# Revit family: RN 32030 Set di allacciamento
name_source: partatom
category: Rohrzubehör
units: mm (PartAtom-declared; Revit-internal decimal feet)

## family parameters
Arbeitsebenenbasiert = Nein
Beim Laden mit Abzugskörper schneiden = Nein
Bemaßung runder Anschluss = Durchmesser verwenden
Gemeinsam genutzt = Nein
Immer vertikal = Ja
Teiletyp = Ventil - Zerlegung in

## types (2) — shared parameters
1.010.00.2 Blattnummer der Richtlinie = 17
1.010.00.3 Ausgabedatum (Monat) der Richtlinie = 201601
1.010.00.4 Herstellername = R. Nussbaum AG
1.010.00.5 Revisionsdatum der Datei = 20190528
1.010.00.6 Webadresse des Herstellers = http://www.nussbaum.ch
1.100.00.3 Sortiernummer für Anzeigereihenfolge = 10
1.100.00.4 Produktbezeichnung = Wasseraufbereitungsarmaturen
1.960/3L.00.8 Link (URL) = https://www.nussbaum.ch
17.700.00.4 Armaturentyp = 1
17.700.00.6 kvs-Wert [m3/h] = 3
17.700.00.7 Maximale Betriebstemperatur TB [°C] = 60
17.700.00.8 Maximaler Betriebsdruck (Arbeitsdruck) ps [1.0 · 105 Pa] = 16
CONNECTOR0_dZ_01 = 70 mm  [stored 0.229659 ft]
CONNECTOR1_dX_00 = 70 mm  [stored 0.229659 ft]
CONNECTOR1_ref_dX = 70 mm  [stored 0.229659 ft]
Connector Visibility = Nein
EnclosingSpace Visibility = Nein
Hersteller = R. Nussbauzm AG
URL = https://www.nussbaum.ch

## per-type parameters (varying)
| type | 1.800.00.3 TGA-Nummer | 1.810.00.3 Hersteller-Bestellnummer | 1.810.00.4 DATANORM-Nummer | 1.810.00.5 StLB-Nummer | 1.810.00.6 GTIN-Nummer | 17.700.00.30 Produktbeschreibung | 17.700.00.5 Nennweite DN | CONNECTOR0_DIAMETER_dZ_0r | CONNECTOR0_dZ_00 | CONNECTOR0_ref_dZ | CONNECTOR1_DIAMETER_dX_0r | CONNECTOR1_dX_01 | Modell | R. Nussbaum AG 32030.06 de Visibility | R. Nussbaum AG 32030.07 de Visibility | Typenkommentare |
| DN 25 | 01000200000000000000000000000200700000000000000001???00000 | 32030.06 | 32030.06 | 618.165 | 7612945007513 | 32030.06, Anschlussgarnitur, zu Stand-Wassererwärmer, DN=25, Rp=1 | 25 | 25 mm  [stored 0.082021 ft] | 53 mm | 53 mm | 40 mm | 59 mm | 32030.06 | Ja | Nein | Set di allacciamentoDN 25 |
| DN 32 | 01000200000000000000000000000200700000000000000002???00000 | 32030.07 | 32030.07 | 618.166 | 7612945007520 | 32030.07, Anschlussgarnitur, zu Stand-Wassererwärmer, DN=32, Rp=1¼ | 32 | 32 mm | 51 mm | 51 mm | 50 mm | 60 mm | 32030.07 | Nein | Ja | Set di allacciamentoDN 32 |

note: [stored X ft] marks values corroborated as IEEE doubles in the binary element streams (Revit-internal decimal feet)

## geometry (parser evidence)
native form markers: Sweep x2
no freeform markers — native parametric forms only
